# Revit family: EZTA(24x16)+ with Hot Water Coil
name_source: partatom
category: Mechanical Equipment
revit_build: Autodesk Revit 2018 (Build: 20170223_1515(x64)
units: mm (PartAtom-declared; Revit-internal decimal feet)

## family parameters
Always vertical = Yes
Cut with Voids When Loaded = No
Part Type = Normal
Room Calculation Point = No
Round Connector Dimension = Use Radius
Shared = No
Work Plane-Based = No

## types (12) — shared parameters
Controller Depth = 7 1/8"
Controller Length = 14 7/32"
Controller Offset = 3"
Description = SINGLE DUCT AIR TERMINAL WITH INTEGRAL ATTENUATOR JUMBO HOT WATER HEATING COIL
Duct Discharge Height = 18"
Duct Discharge Width = 38"
Duct Inlet Dia = 16"
HWC Conn "B" = 1 3/4"
HWC Conn "D" = 17/32"
HWC Conn "E" = 1 5/32"
HWC Conn Diameter = 1"
HWC Conn Length = 4 1/2"
HWC Depth "A" = 7"
Height = 18"
Inlet Center = 9"
Inlet Depth = 5 7/16"
Length = 39 1/2"
Manufacturer = Anemostat Products
Model = EZTA+ With Hot Water Coil
URL = https://www.anemostat-hvac.com
Width = 38"

## per-type parameters (varying)
| type | Coil Thickness | Controller Center | Controller Left | Controller Right | HWC Conn "C" | HWC Conn Radius |
| EZTA(24x16)+ with 2 Row HWC & NO Controller | -5" | 5 9/16" | No | No | 2 27/32" | 0" |
| EZTA(24x16)+ with 1 Row HWC & NO Controller | -5" | 5 11/16" | No | No | 3 1/4" | 0" |
| EZTA(24x16)+ with 3 Row HWC & NO Controller | -6" | 5 11/16" | No | No | 3 27/32" | 1" |
| EZTA(24x16)+ with 4 Row HWC & NO Controller | -6" | 5 11/16" | No | No | 3 27/32" | 1" |
| EZTA(24x16)+ with 2 Row HWC & Controller RH | -5" | 5 9/16" | No | Yes | 2 27/32" | 0" |
| EZTA(24x16)+ with 1 Row HWC & Controller RH | -5" | 5 11/16" | No | Yes | 3 1/4" | 0" |
| EZTA(24x16)+ with 4 Row HWC & Controller RH | -6" | 5 11/16" | No | Yes | 3 27/32" | 1" |
| EZTA(24x16)+ with 3 Row HWC & Controller RH | -6" | 5 11/16" | No | Yes | 3 27/32" | 1" |
| EZTA(24x16)+ with 1 Row HWC & Controller LH | -5" | 5 11/16" | Yes | No | 3 1/4" | 0" |
| EZTA(24x16)+ with 2 Row HWC & Controller LH | -5" | 5 9/16" | Yes | No | 2 27/32" | 0" |
| EZTA(24x16)+ with 3 Row HWC & Controller LH | -6" | 5 11/16" | Yes | No | 3 27/32" | 1" |
| EZTA(24x16)+ with 4 Row HWC & Controller LH | -6" | 5 11/16" | Yes | No | 3 27/32" | 1" |

## geometry (parser evidence)
native form markers: Sweep x2
no freeform markers — native parametric forms only
